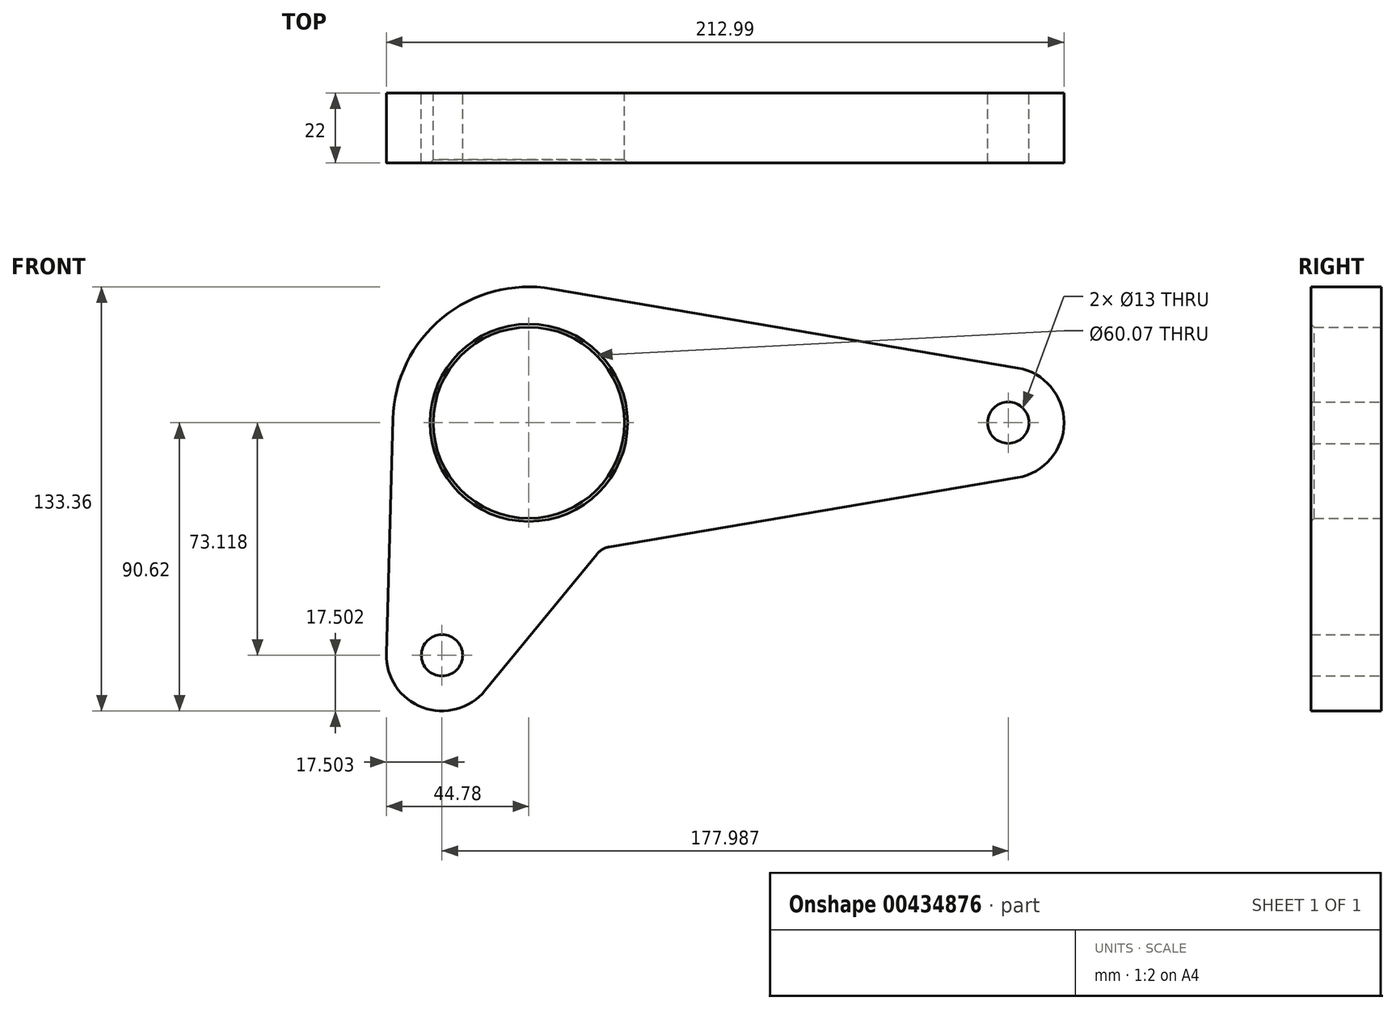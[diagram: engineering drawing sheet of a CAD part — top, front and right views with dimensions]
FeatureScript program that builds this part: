
annotation { "Feature Type Name" : "Feature", "Feature Type Description" : "" }
export const myFeature = defineFeature(function(context is Context, id is Id, definition is map)
    precondition{}
    {
        {
            var Q0;
            Q0=qCreatedBy(makeId("Front.planeOp"),FACE);
            var sketch = newSketch(context, id + "F0", { "sketchPlane" : qUnion([Q0])});
            skCircle(sketch, "E0", {"center": v(0, 0) * mm, "radius": 30.04 * mm});
            skPoint(sketch, "E1", {"position": v(150.71, 0) * mm});
            skPoint(sketch, "E2", {"position": v(-27.28, -73.12) * mm});
            skCircle(sketch, "E3", {"center": v(150.71, 0) * mm, "radius": 6.5 * mm});
            skCircle(sketch, "E4", {"center": v(-27.28, -73.12) * mm, "radius": 6.5 * mm});
            skLineSegment(sketch, "E5", {"start": v(7.16, 42.13) * mm, "end": v(153.64, 17.25) * mm});
            skLineSegment(sketch, "E6", {"start": v(153.64, -17.25) * mm, "end": v(25.27, -39.06) * mm});
            skLineSegment(sketch, "E7", {"start": v(-13.74, -84.2) * mm, "end": v(21.42, -41.3) * mm});
            skLineSegment(sketch, "E8", {"start": v(-44.77, -72.63) * mm, "end": v(-42.72, 1.19) * mm});
            skArc(sketch, "E9.filletArc", {"start": v(25.27, -39.06) * mm, "mid": v(23.14, -39.83) * mm, "end": v(21.42, -41.3) * mm});
            skArc(sketch, "E10.filletArc", {"start": v(7.16, 42.13) * mm, "mid": v(-27.12, 33.03) * mm, "end": v(-42.72, 1.19) * mm});
            skArc(sketch, "E11.filletArc", {"start": v(153.64, -17.25) * mm, "mid": v(168.21, 0) * mm, "end": v(153.64, 17.25) * mm});
            skArc(sketch, "E12.filletArc", {"start": v(-44.77, -72.63) * mm, "mid": v(-33.4, -89.51) * mm, "end": v(-13.74, -84.2) * mm});
            skSolve(sketch);
        }
        {
            var Q0;
            Q0=makeQuery(id+"F0.imprint","IMPRINT",FACE,{"disambiguationData":[TD([[makeQuery(id+"F0.imprint","IMPRINT",EDGE,{"derivedFrom":sQuery(id+"F0.wireOp",EDGE,"E0")}),-1.0]])]});
            extrude(context, id + "F1", {"entities" : qUnion([Q0]), "endBound" : BoundingType.SYMMETRIC, "depth" : 22 * mm});
        }
        {
            var Q0;
            Q0=makeQuery(id+"F1.opExtrude","CAP_EDGE",EDGE,{"disambiguationData":[OSD([sQuery(id+"F0.wireOp",EDGE,"E0")])],"isStart":false});
            chamfer(context, id + "F2", {"entities" : qUnion([Q0]), "width" : 1 * mm, "tangentPropagation" : true});
        }
    });
